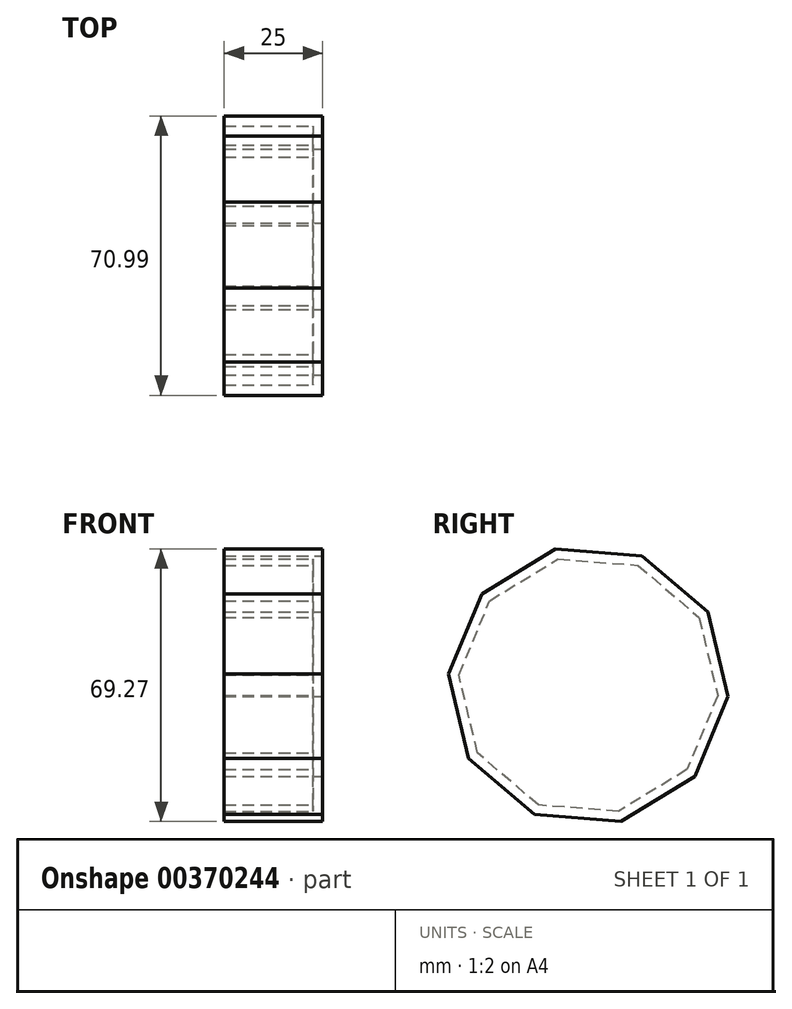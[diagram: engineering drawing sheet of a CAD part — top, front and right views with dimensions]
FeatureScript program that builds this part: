
annotation { "Feature Type Name" : "Feature", "Feature Type Description" : "" }
export const myFeature = defineFeature(function(context is Context, id is Id, definition is map)
    precondition{}
    {
        {
            var Q0;
            Q0=qCreatedBy(makeId("Right.planeOp"),FACE);
            var sketch = newSketch(context, id + "F0", { "sketchPlane" : qUnion([Q0])});
            skCircle(sketch, "E0.cCircle", {"center": v(-77.25, 55.03) * mm, "radius": 33.87 * mm, "construction": true});
            skLineSegment(sketch, "E0.0", {"start": v(-41.76, 52.2) * mm, "end": v(-50.2, 31.88) * mm});
            skLineSegment(sketch, "E0.1", {"start": v(-50.2, 31.88) * mm, "end": v(-68.98, 20.4) * mm});
            skLineSegment(sketch, "E0.2", {"start": v(-68.98, 20.4) * mm, "end": v(-90.91, 22.14) * mm});
            skLineSegment(sketch, "E0.3", {"start": v(-90.91, 22.14) * mm, "end": v(-107.63, 36.45) * mm});
            skLineSegment(sketch, "E0.4", {"start": v(-107.63, 36.45) * mm, "end": v(-112.75, 57.86) * mm});
            skLineSegment(sketch, "E0.5", {"start": v(-112.75, 57.86) * mm, "end": v(-104.3, 78.18) * mm});
            skLineSegment(sketch, "E0.6", {"start": v(-104.3, 78.18) * mm, "end": v(-85.53, 89.66) * mm});
            skLineSegment(sketch, "E0.7", {"start": v(-85.53, 89.66) * mm, "end": v(-63.6, 87.91) * mm});
            skLineSegment(sketch, "E0.8", {"start": v(-63.6, 87.91) * mm, "end": v(-46.87, 73.6) * mm});
            skLineSegment(sketch, "E0.9", {"start": v(-46.87, 73.6) * mm, "end": v(-41.76, 52.2) * mm});
            skPoint(sketch, "E0.0.midPoint", {"position": v(-45.98, 42.04) * mm});
            skCircle(sketch, "E1.cCircle", {"center": v(-77.25, 55.03) * mm, "radius": 18.73 * mm, "construction": true});
            skLineSegment(sketch, "E1.0", {"start": v(-90.06, 40.07) * mm, "end": v(-96.4, 50.45) * mm});
            skLineSegment(sketch, "E1.1", {"start": v(-96.4, 50.45) * mm, "end": v(-95.44, 62.58) * mm});
            skLineSegment(sketch, "E1.2", {"start": v(-95.44, 62.58) * mm, "end": v(-87.53, 71.83) * mm});
            skLineSegment(sketch, "E1.3", {"start": v(-87.53, 71.83) * mm, "end": v(-75.69, 74.66) * mm});
            skLineSegment(sketch, "E1.4", {"start": v(-75.69, 74.66) * mm, "end": v(-64.45, 69.99) * mm});
            skLineSegment(sketch, "E1.5", {"start": v(-64.45, 69.99) * mm, "end": v(-58.1, 59.6) * mm});
            skLineSegment(sketch, "E1.6", {"start": v(-58.1, 59.6) * mm, "end": v(-59.07, 47.47) * mm});
            skLineSegment(sketch, "E1.7", {"start": v(-59.07, 47.47) * mm, "end": v(-66.98, 38.23) * mm});
            skLineSegment(sketch, "E1.8", {"start": v(-66.98, 38.23) * mm, "end": v(-78.82, 35.4) * mm});
            skLineSegment(sketch, "E1.9", {"start": v(-78.82, 35.4) * mm, "end": v(-90.06, 40.07) * mm});
            skPoint(sketch, "E1.0.midPoint", {"position": v(-93.23, 45.26) * mm});
            skSolve(sketch);
        }
        {
            var Q0;
            Q0=makeQuery(id+"F0.imprint","IMPRINT",FACE,{"disambiguationData":[TD([[makeQuery(id+"F0.imprint","IMPRINT",EDGE,{"derivedFrom":sQuery(id+"F0.wireOp",EDGE,"E0.0")}),-1.0]])]});
            var Q1;
            Q1=makeQuery(id+"F0.imprint","IMPRINT",FACE,{"disambiguationData":[TD([[makeQuery(id+"F0.imprint","IMPRINT",EDGE,{"derivedFrom":sQuery(id+"F0.wireOp",EDGE,"E1.0")}),-1.0]])]});
            extrude(context, id + "F1", {"entities" : qUnion([Q0, Q1]), "oppositeDirection" : true, "depth" : 25 * mm});
        }
        {
            var Q0;
            Q0=makeQuery(id+"F1.opExtrude","CAP_FACE",FACE,{"disambiguationData":[OSD([sQuery(id+"F0.wireOp",EDGE,"E0.0"),sQuery(id+"F0.wireOp",EDGE,"E0.1"),sQuery(id+"F0.wireOp",EDGE,"E0.2"),sQuery(id+"F0.wireOp",EDGE,"E0.3"),sQuery(id+"F0.wireOp",EDGE,"E0.4"),sQuery(id+"F0.wireOp",EDGE,"E0.5"),sQuery(id+"F0.wireOp",EDGE,"E0.6"),sQuery(id+"F0.wireOp",EDGE,"E0.7"),sQuery(id+"F0.wireOp",EDGE,"E0.8"),sQuery(id+"F0.wireOp",EDGE,"E0.9")])],"isStart":false});
            shell(context, id + "F2", {"entities" : qUnion([Q0]), "thickness" : 2.5 * mm});
        }
    });
